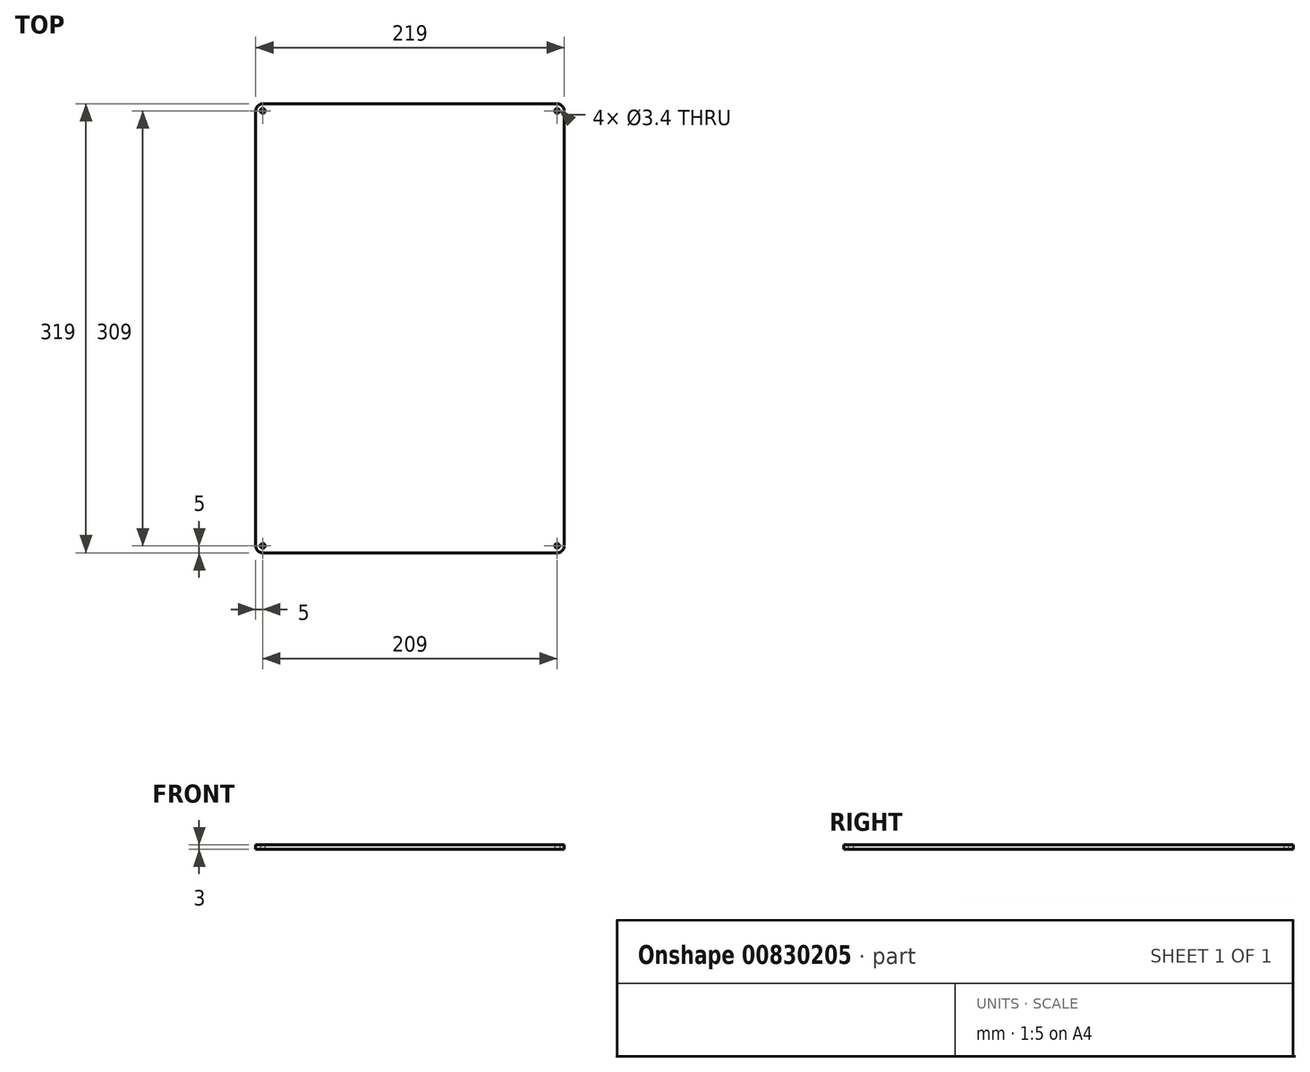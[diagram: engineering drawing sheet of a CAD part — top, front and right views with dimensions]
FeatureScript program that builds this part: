
annotation { "Feature Type Name" : "Feature", "Feature Type Description" : "" }
export const myFeature = defineFeature(function(context is Context, id is Id, definition is map)
    precondition{}
    {
        {
            var Q0;
            Q0=qCreatedBy(makeId("Top.planeOp"),FACE);
            var sketch = newSketch(context, id + "F0", { "sketchPlane" : qUnion([Q0])});
            skLineSegment(sketch, "E0", {"start": v(0, 138.98) * mm, "end": v(0, -196.3) * mm, "construction": true});
            skLineSegment(sketch, "E1", {"start": v(-162.61, 0) * mm, "end": v(192.69, 0) * mm, "construction": true});
            skLineSegment(sketch, "E2.bottom", {"start": v(-104.5, -159.5) * mm, "end": v(104.5, -159.5) * mm});
            skLineSegment(sketch, "E2.top", {"start": v(-104.5, 159.5) * mm, "end": v(104.5, 159.5) * mm});
            skLineSegment(sketch, "E2.left", {"start": v(-109.5, -154.5) * mm, "end": v(-109.5, 154.5) * mm});
            skLineSegment(sketch, "E2.right", {"start": v(109.5, -154.5) * mm, "end": v(109.5, 154.5) * mm});
            skPoint(sketch, "E3.visualSharp", {"position": v(-109.5, -159.5) * mm});
            skArc(sketch, "E3.filletArc", {"start": v(-109.5, -154.5) * mm, "mid": v(-108.04, -158.04) * mm, "end": v(-104.5, -159.5) * mm});
            skPoint(sketch, "E4.visualSharp", {"position": v(109.5, -159.5) * mm});
            skArc(sketch, "E4.filletArc", {"start": v(104.5, -159.5) * mm, "mid": v(108.04, -158.04) * mm, "end": v(109.5, -154.5) * mm});
            skPoint(sketch, "E5.visualSharp", {"position": v(109.5, 159.5) * mm});
            skArc(sketch, "E5.filletArc", {"start": v(109.5, 154.5) * mm, "mid": v(108.04, 158.04) * mm, "end": v(104.5, 159.5) * mm});
            skPoint(sketch, "E6.visualSharp", {"position": v(-109.5, 159.5) * mm});
            skArc(sketch, "E6.filletArc", {"start": v(-104.5, 159.5) * mm, "mid": v(-108.04, 158.04) * mm, "end": v(-109.5, 154.5) * mm});
            skCircle(sketch, "E7", {"center": v(-104.5, 154.5) * mm, "radius": 1.7 * mm});
            skCircle(sketch, "E8.MirrorC", {"center": v(104.5, 154.5) * mm, "radius": 1.7 * mm});
            skCircle(sketch, "E9.MirrorC", {"center": v(-104.5, -154.5) * mm, "radius": 1.7 * mm});
            skCircle(sketch, "E10.MirrorC", {"center": v(104.5, -154.5) * mm, "radius": 1.7 * mm});
            skSolve(sketch);
        }
        {
            var Q0;
            Q0=qSketchRegion(id+"F0",true);
            extrude(context, id + "F1", {"entities" : qUnion([Q0]), "depth" : 3 * mm, "offsetDistance" : 25 * mm});
        }
    });
